# Revit family: QF_ELECTROLUXPROFESSIONAL_137010_ALS772
name_source: partatom
category: Attrezzature speciali
units: mm (PartAtom-declared; Revit-internal decimal feet)

## family parameters
Basato su piano di lavoro = No
Condiviso = No
Punto di calcolo locali = No
Quota connettore circolare = Usa diametro
Sempre verticale = Sì
Taglio con vuoti quando caricato = No
Tipo di parte = Normale

## types (1)
- Standard
    Accessory = Sì
    Cold Water Size = 0 mm
    Compressed Air Pressure = 0.0 Pa
    Compressed Air Size = 0 mm
    Compressed Air Volume = 0.0 L/s
    Condensate Return Size = 0 mm
    Cycle = 0 Hz
    Depth Actual = 373 mm  [stored 1.22375 ft]
    Descrizione = ALUM.LINEAR SHELV.-POLY.TIERS-373X772MM
    Direct Waste Size = 0 mm
    Gas Input Pressure = 0
    Gas KW = 0
    Gas Size = 0 mm
    HP = 0 HP
    Height Actual = 1700 mm  [stored 5.57743 ft]
    Hot Water Size = 0 mm
    Item Number = 137010
    Length Actual = 772 mm  [stored 2.53281 ft]
    Modello = ALS772
    Phase = 0
    Produttore = Electrolux Professional
    Prospetto di default = 0 mm  [stored 0 ft]
    Refrigerant Compressor Remote = Sì
    Refrigeration Liquid Line Size = 0 mm  [stored 0 ft]
    Refrigeration Suction Line Size = 0 mm  [stored 0 ft]
    Steam Consumption per Hour = 0
    Steam Supply Maximum Pressure = 0.0 Pa
    Steam Supply Minimum Pressure = 0.0 Pa
    Steam Supply Size = 0 mm
    URL = https://www.electroluxprofessional.com
    URL Manufacturer = https://www.electroluxprofessional.com
    Volts = 0 V
    Watts = 0 W
    Weight = 16.00 kg

note: source unit labels omitted for Gas Input Pressure — the stored unit's dimension contradicts the parameter name (converter mislabeling)

note: [stored X ft] marks values corroborated as IEEE doubles in the binary element streams (Revit-internal decimal feet)

## geometry (parser evidence)
native form markers: Sweep x5
no freeform markers — native parametric forms only
